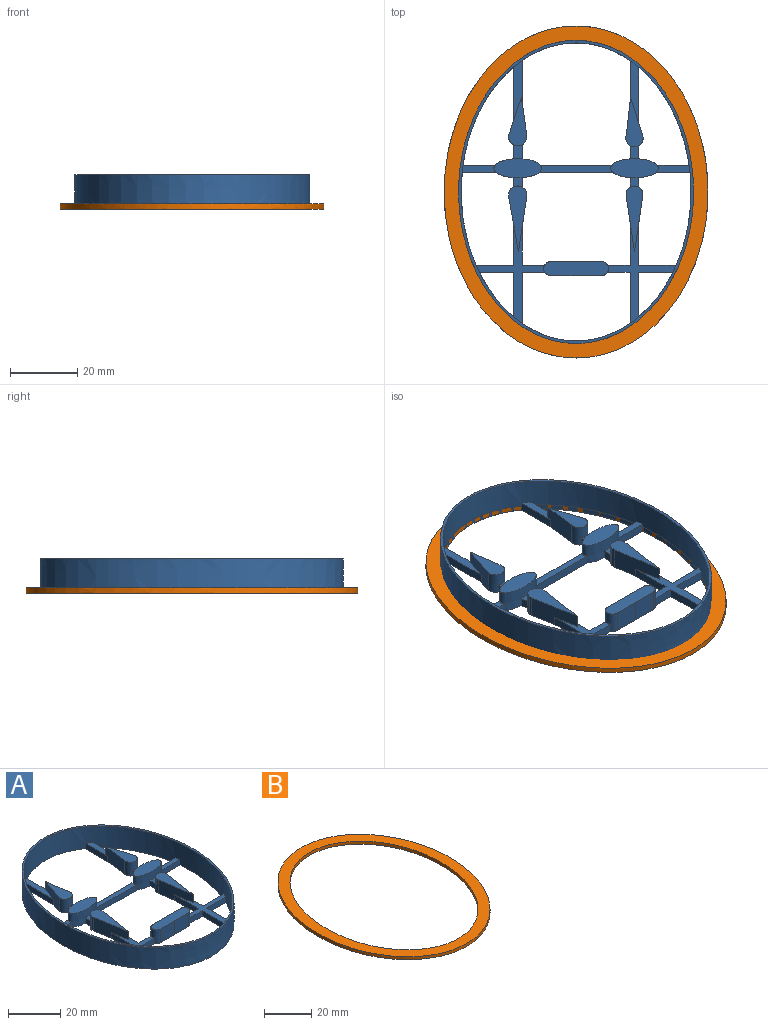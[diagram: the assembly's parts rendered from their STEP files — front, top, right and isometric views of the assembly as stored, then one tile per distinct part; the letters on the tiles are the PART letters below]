
ASSEMBLY  parts=2 mates=1
PART A: 84 faces, bbox 70.1x90.4x10.2 mm
  f0: extruded ~88.9x68.58mm, area 2469.4mm2, adj f2,f3,f8,f9,f10,f28,f29,f30
  f1: extruded ~90.42x70.1mm, area 2572.3mm2, adj f2,f3
  f2: plane 90.44x70.12mm, normal (0,0,1), area 191.5mm2, adj f0,f1
  f3: plane 90.44x70.12mm, normal (0,0,-1), area 971.1mm2, adj f0,f1,f4,f5,f6,f8,f9,f11
  f4: cylinder r=2.58mm len=6.35mm, axis (0,0,-1), area 55.1mm2, adj f3,f5,f6,f7,f11,f12,f13
  f5: plane 11.38x6.35mm, normal (0.95,0.3,0), area 55.9mm2, adj f3,f4,f6,f7,f8,f10
  f6: plane 11.36x6.35mm, normal (-0.99,0.11,0), area 69.4mm2, adj f3,f4,f5,f7,f9,f10
  f7: plane 14.74x5.17mm, normal (0,0,1), area 42.4mm2, adj f4,f5,f6
  f8: plane 16.63x2.54mm, normal (1,0,0), area 42.2mm2, adj f0,f3,f5,f10
  f9: plane 12.31x2.54mm, normal (-1,0,0), area 31.3mm2, adj f0,f3,f6,f10
  f10: plane 18.55x2.52mm, normal (0,0,1), area 34.5mm2, adj f0,f5,f6,f8,f9
  f11: plane 3.86x2.54mm, normal (1,0,0), area 9.8mm2, adj f3,f4,f13,f14
  f12: plane 3.9x2.54mm, normal (-1,0,0), area 9.9mm2, adj f3,f4,f13,f14
  f13: plane 3.9x2.52mm, normal (0,0,1), area 9.1mm2, adj f4,f11,f12,f14
  f14: extruded ~14.21x6.35mm, area 183mm2, adj f3,f11,f12,f13,f15,f16,f17,f18
  f15: plane 14.21x5.7mm, normal (0,0,1), area 63.7mm2, adj f14
  f16: plane 21.42x2.54mm, normal (0,1,0), area 54.4mm2, adj f3,f14,f18,f19
  f17: plane 21.79x2.54mm, normal (0,-1,0), area 55.4mm2, adj f3,f14,f18,f19
  f18: plane 21.79x2.08mm, normal (0,0,1), area 43.5mm2, adj f14,f16,f17,f19
  f19: extruded ~14.21x6.35mm, area 183mm2, adj f3,f16,f17,f18,f20,f21,f22,f23
  f20: plane 14.21x5.7mm, normal (0,0,1), area 63.7mm2, adj f19
  f21: plane 4.26x2.54mm, normal (1,0,0), area 10.8mm2, adj f3,f19,f23,f25
  f22: plane 4.22x2.54mm, normal (-1,0,0), area 10.7mm2, adj f3,f19,f23,f25
  f23: plane 4.26x2.52mm, normal (0,0,1), area 10.1mm2, adj f19,f21,f22,f25
  f24: plane 11.31x6.35mm, normal (-0.95,0.32,0), area 57.3mm2, adj f3,f25,f26,f27,f29,f30
  f25: cylinder r=2.75mm len=6.35mm, axis (0,0,-1), area 53.1mm2, adj f3,f21,f22,f23,f24,f26,f27
  f26: plane 11.31x6.35mm, normal (0.99,0.14,0), area 69mm2, adj f3,f24,f25,f27,f28,f30
  f27: plane 14.45x5.49mm, normal (0,0,1), area 44.7mm2, adj f24,f25,f26
  f28: plane 12.36x2.54mm, normal (1,0,0), area 31.4mm2, adj f0,f3,f26,f30
  f29: plane 15.95x2.54mm, normal (-1,0,0), area 40.5mm2, adj f0,f3,f24,f30
  f30: plane 17.87x2.52mm, normal (0,0,1), area 33.4mm2, adj f0,f24,f26,f28,f29
  f31: plane 9.61x2.54mm, normal (0,1,0), area 24.4mm2, adj f0,f3,f19,f33
  f32: plane 10.05x2.54mm, normal (0,-1,0), area 25.5mm2, adj f0,f3,f19,f33
  f33: plane 10.05x2.08mm, normal (0,0,1), area 19.8mm2, adj f0,f19,f31,f32
  f34: plane 2.86x2.54mm, normal (-1,0,0), area 7.3mm2, adj f3,f14,f36,f38
  f35: plane 2.8x2.54mm, normal (1,0,0), area 7.1mm2, adj f3,f14,f36,f48
  f36: plane 2.86x2.52mm, normal (0,0,1), area 6.5mm2, adj f14,f34,f35,f37,f38,f48
  f37: plane 3.81x0.01mm, normal (0,1,0), area 0mm2, adj f36,f38,f48,f49
  f38: cylinder r=2.53mm len=6.35mm, axis (0,0,-1), area 17.9mm2, adj f3,f34,f36,f37,f44,f49
  f39: cylinder r=2.75mm len=2.54mm, axis (0,0,-1), area 1.6mm2, adj f3,f42,f79
  f40: plane 2.76x2.54mm, normal (-1,0,0), area 7mm2, adj f3,f19,f42,f43
  f41: plane 2.8x2.54mm, normal (1,0,0), area 7.1mm2, adj f3,f19,f42,f78
  f42: plane 2.8x2.52mm, normal (0,0,1), area 6.4mm2, adj f19,f39,f40,f41,f43,f78
  f43: cylinder r=2.75mm len=6.35mm, axis (0,0,-1), area 20.4mm2, adj f3,f40,f42,f76,f79,f80
  f44: plane 6.35x1.21mm, normal (-1,0,0), area 7.7mm2, adj f3,f38,f45,f49
  f45: plane 16.33x6.35mm, normal (-0.99,-0.15,0), area 82.6mm2, adj f3,f44,f46,f49,f55,f58
  f46: plane 16.31x6.35mm, normal (0.99,-0.15,0), area 84mm2, adj f3,f45,f47,f49,f54,f58
  f47: plane 6.35x1.24mm, normal (1,0,0), area 7.8mm2, adj f3,f46,f48,f49
  f48: cylinder r=2.53mm len=6.35mm, axis (0,0,-1), area 18.1mm2, adj f3,f35,f36,f37,f47,f49
  f49: plane 19.47x4.92mm, normal (0,0,1), area 53.2mm2, adj f37,f38,f44,f45,f46,f47,f48
  f50: plane 15.31x2.54mm, normal (-1,0,0), area 38.9mm2, adj f0,f3,f57,f58
  f51: plane 13.39x2.54mm, normal (1,0,0), area 34mm2, adj f0,f3,f52,f58
  f52: plane 10.26x2.54mm, normal (0,-1,0), area 26.1mm2, adj f0,f3,f51,f58
  f53: plane 11.21x2.54mm, normal (0,1,0), area 28.5mm2, adj f0,f3,f54,f58
  f54: plane 12.24x2.54mm, normal (1,0,0), area 31.1mm2, adj f3,f46,f53,f58
  f55: plane 12.82x2.54mm, normal (-1,0,0), area 32.6mm2, adj f3,f45,f56,f58
  f56: plane 6.71x2.54mm, normal (0,1,0), area 17mm2, adj f3,f55,f58,f61
  f57: plane 6.73x2.54mm, normal (0,-1,0), area 17.1mm2, adj f3,f50,f58,f61
  f58: plane 30.18x20.46mm, normal (0,0,1), area 97.9mm2, adj f0,f45,f46,f50,f51,f52,f53,f54
  f59: cylinder r=2.05mm len=6.35mm, axis (0,0,-1), area 35.4mm2, adj f3,f62,f63,f64,f69,f70,f73
  f60: plane 7.62x6.35mm, normal (0,-1,0), area 48.4mm2, adj f3,f61,f63,f64
  f61: cylinder r=2.05mm len=6.35mm, axis (0,0,-1), area 35.4mm2, adj f3,f56,f57,f58,f60,f62,f64
  f62: plane 15.24x6.35mm, normal (0,1,0), area 96.8mm2, adj f3,f59,f61,f64
  f63: plane 7.62x6.35mm, normal (0,-1,0), area 48.4mm2, adj f3,f59,f60,f64
  f64: plane 19.34x4.1mm, normal (0,0,1), area 75.6mm2, adj f59,f60,f61,f62,f63
  f65: plane 11.21x2.54mm, normal (0,1,0), area 28.5mm2, adj f0,f3,f72,f73
  f66: plane 10.26x2.54mm, normal (0,-1,0), area 26.1mm2, adj f0,f3,f67,f73
  f67: plane 13.39x2.54mm, normal (-1,0,0), area 34mm2, adj f0,f3,f66,f73
  f68: plane 15.31x2.54mm, normal (1,0,0), area 38.9mm2, adj f0,f3,f69,f73
  f69: plane 6.74x2.54mm, normal (0,-1,0), area 17.1mm2, adj f3,f59,f68,f73
  f70: plane 6.72x2.54mm, normal (0,1,0), area 17.1mm2, adj f3,f59,f71,f73
  f71: plane 11.28x2.54mm, normal (1,0,0), area 28.6mm2, adj f3,f70,f73,f75
  f72: plane 12.12x2.54mm, normal (-1,0,0), area 30.8mm2, adj f3,f65,f73,f74
  f73: plane 29.48x20.47mm, normal (0,0,1), area 96.9mm2, adj f0,f59,f65,f66,f67,f68,f69,f70
  f74: plane 16.32x6.35mm, normal (-0.98,-0.18,0), area 84.7mm2, adj f3,f72,f73,f75,f76,f80
  f75: plane 16.32x6.35mm, normal (0.99,-0.15,0), area 86.6mm2, adj f3,f71,f73,f74,f77,f80
  f76: plane 6.35x0.84mm, normal (-1,0,0), area 5.3mm2, adj f3,f43,f74,f80
  f77: plane 6.35x0.84mm, normal (1,0,0), area 5.3mm2, adj f3,f75,f78,f80
  f78: cylinder r=2.75mm len=6.35mm, axis (0,0,-1), area 20.1mm2, adj f3,f41,f42,f77,f79,f80
  f79: plane 6.35x0.62mm, normal (0,1,0), area 3.9mm2, adj f3,f39,f43,f78,f80
  f80: plane 19.47x5.44mm, normal (0,0,1), area 58.5mm2, adj f43,f74,f75,f76,f77,f78,f79
  f81: plane 10.04x2.54mm, normal (0,-1,0), area 25.5mm2, adj f0,f3,f14,f83
  f82: plane 9.6x2.54mm, normal (0,1,0), area 24.4mm2, adj f0,f3,f14,f83
  f83: plane 10.04x2.08mm, normal (0,0,1), area 19.7mm2, adj f0,f14,f81,f82
PART B: 4 faces, bbox 78.8x99.1x1.5 mm
  f0: extruded ~88.9x68.58mm, area 378.6mm2, adj f2,f3
  f1: extruded ~99.06x78.74mm, area 427.2mm2, adj f2,f3
  f2: plane 99.08x78.76mm, normal (0,0,1), area 1343.4mm2, adj f0,f1
  f3: plane 99.08x78.76mm, normal (0,0,-1), area 1343.4mm2, adj f0,f1
PLACE A t=(0,0,-1.27)mm
PLACE B rot(axis=(1,0,0),180deg) t=(0.89,2.09,0.25)mm
MATE fastened B.f2 <-> A.f3  axis (0,0,-1) through (0.89,1.57,-1.27)mm
